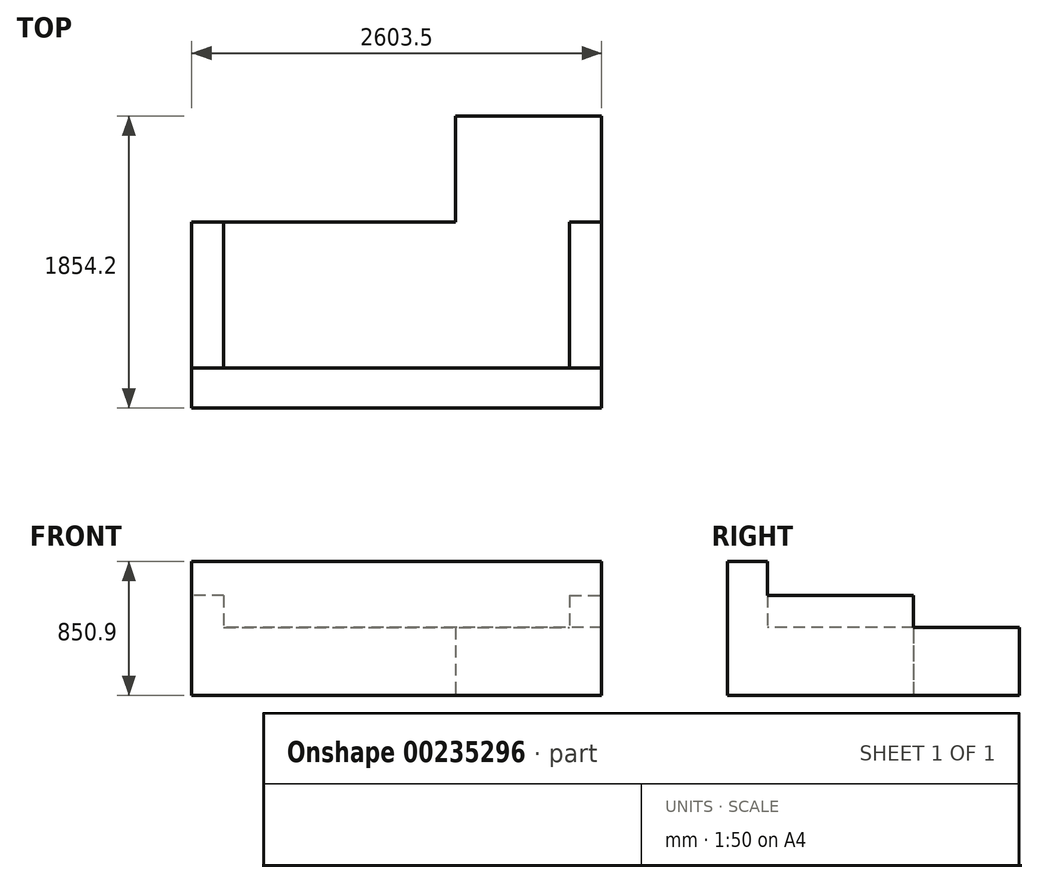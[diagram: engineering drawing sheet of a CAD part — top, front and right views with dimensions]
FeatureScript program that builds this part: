
annotation { "Feature Type Name" : "Feature", "Feature Type Description" : "" }
export const myFeature = defineFeature(function(context is Context, id is Id, definition is map)
    precondition{}
    {
        {
            var Q0;
            Q0=qCreatedBy(makeId("Top.planeOp"),FACE);
            var sketch = newSketch(context, id + "F0", { "sketchPlane" : qUnion([Q0])});
            skLineSegment(sketch, "E0", {"start": v(-1301.75, 254) * mm, "end": v(-1301.75, -927.1) * mm});
            skLineSegment(sketch, "E1", {"start": v(-1301.75, -927.1) * mm, "end": v(1301.75, -927.1) * mm});
            skLineSegment(sketch, "E2", {"start": v(1301.75, -927.1) * mm, "end": v(1301.75, 927.1) * mm});
            skLineSegment(sketch, "E3", {"start": v(1301.75, 927.1) * mm, "end": v(374.65, 927.1) * mm});
            skLineSegment(sketch, "E4", {"start": v(374.65, 254) * mm, "end": v(374.65, 927.1) * mm});
            skLineSegment(sketch, "E5", {"start": v(374.65, 254) * mm, "end": v(-1301.75, 254) * mm});
            skLineSegment(sketch, "E6", {"start": v(1301.75, 0) * mm, "end": v(-1301.75, 0) * mm, "construction": true});
            skSolve(sketch);
        }
        {
            var Q0;
            Q0=qSketchRegion(id+"F0",true);
            extrude(context, id + "F1", {"entities" : qUnion([Q0]), "depth" : 431.8 * mm});
        }
        {
            var Q0;
            Q0=makeQuery(id+"F1.opExtrude","CAP_FACE",FACE,{"disambiguationData":[OSD([sQuery(id+"F0.wireOp",EDGE,"E0"),sQuery(id+"F0.wireOp",EDGE,"E1"),sQuery(id+"F0.wireOp",EDGE,"E2"),sQuery(id+"F0.wireOp",EDGE,"E3"),sQuery(id+"F0.wireOp",EDGE,"E4"),sQuery(id+"F0.wireOp",EDGE,"E5")])],"isStart":false});
            var sketch = newSketch(context, id + "F2", { "sketchPlane" : qUnion([Q0])});
            skLineSegment(sketch, "E7.0", {"start": v(-1301.75, -673.1) * mm, "end": v(1301.75, -673.1) * mm});
            skLineSegment(sketch, "E8", {"start": v(-1047.75, 254) * mm, "end": v(-1301.75, 254) * mm});
            skLineSegment(sketch, "E9", {"start": v(1301.75, -673.1) * mm, "end": v(1301.75, -927.1) * mm});
            skLineSegment(sketch, "E10.1", {"start": v(-1301.75, -927.1) * mm, "end": v(1301.75, -927.1) * mm});
            skLineSegment(sketch, "E11", {"start": v(-1301.75, -673.1) * mm, "end": v(-1301.75, -927.1) * mm});
            skSolve(sketch);
        }
        {
            var Q0;
            Q0=qSketchRegion(id+"F2",true);
            extrude(context, id + "F3", {"entities" : qUnion([Q0]), "operationType" : NewBodyOperationType.ADD, "depth" : 419.1 * mm});
        }
        {
            var Q0;
            Q0=makeQuery(id+"F1.opExtrude","CAP_FACE",FACE,{"disambiguationData":[OSD([sQuery(id+"F0.wireOp",EDGE,"E0"),sQuery(id+"F0.wireOp",EDGE,"E1"),sQuery(id+"F0.wireOp",EDGE,"E2"),sQuery(id+"F0.wireOp",EDGE,"E3"),sQuery(id+"F0.wireOp",EDGE,"E4"),sQuery(id+"F0.wireOp",EDGE,"E5")])],"isStart":false});
            var sketch = newSketch(context, id + "F4", { "sketchPlane" : qUnion([Q0])});
            skLineSegment(sketch, "E12.bottom", {"start": v(1301.75, 254) * mm, "end": v(1098.55, 254) * mm});
            skLineSegment(sketch, "E12.top", {"start": v(1301.75, -673.1) * mm, "end": v(1098.55, -673.1) * mm});
            skLineSegment(sketch, "E12.left", {"start": v(1301.75, 254) * mm, "end": v(1301.75, -673.1) * mm});
            skLineSegment(sketch, "E12.right", {"start": v(1098.55, 254) * mm, "end": v(1098.55, -673.1) * mm});
            skLineSegment(sketch, "E13.top", {"start": v(-1301.75, -673.1) * mm, "end": v(-1098.55, -673.1) * mm});
            skLineSegment(sketch, "E13.left", {"start": v(-1301.75, 254) * mm, "end": v(-1301.75, -673.1) * mm});
            skLineSegment(sketch, "E13.right", {"start": v(-1098.55, 254) * mm, "end": v(-1098.55, -673.1) * mm});
            skLineSegment(sketch, "E14", {"start": v(-1301.75, 254) * mm, "end": v(-1098.55, 254) * mm});
            skSolve(sketch);
        }
        {
            var Q0;
            Q0=qSketchRegion(id+"F4",true);
            extrude(context, id + "F5", {"entities" : qUnion([Q0]), "operationType" : NewBodyOperationType.ADD, "depth" : 203.2 * mm});
        }
    });
